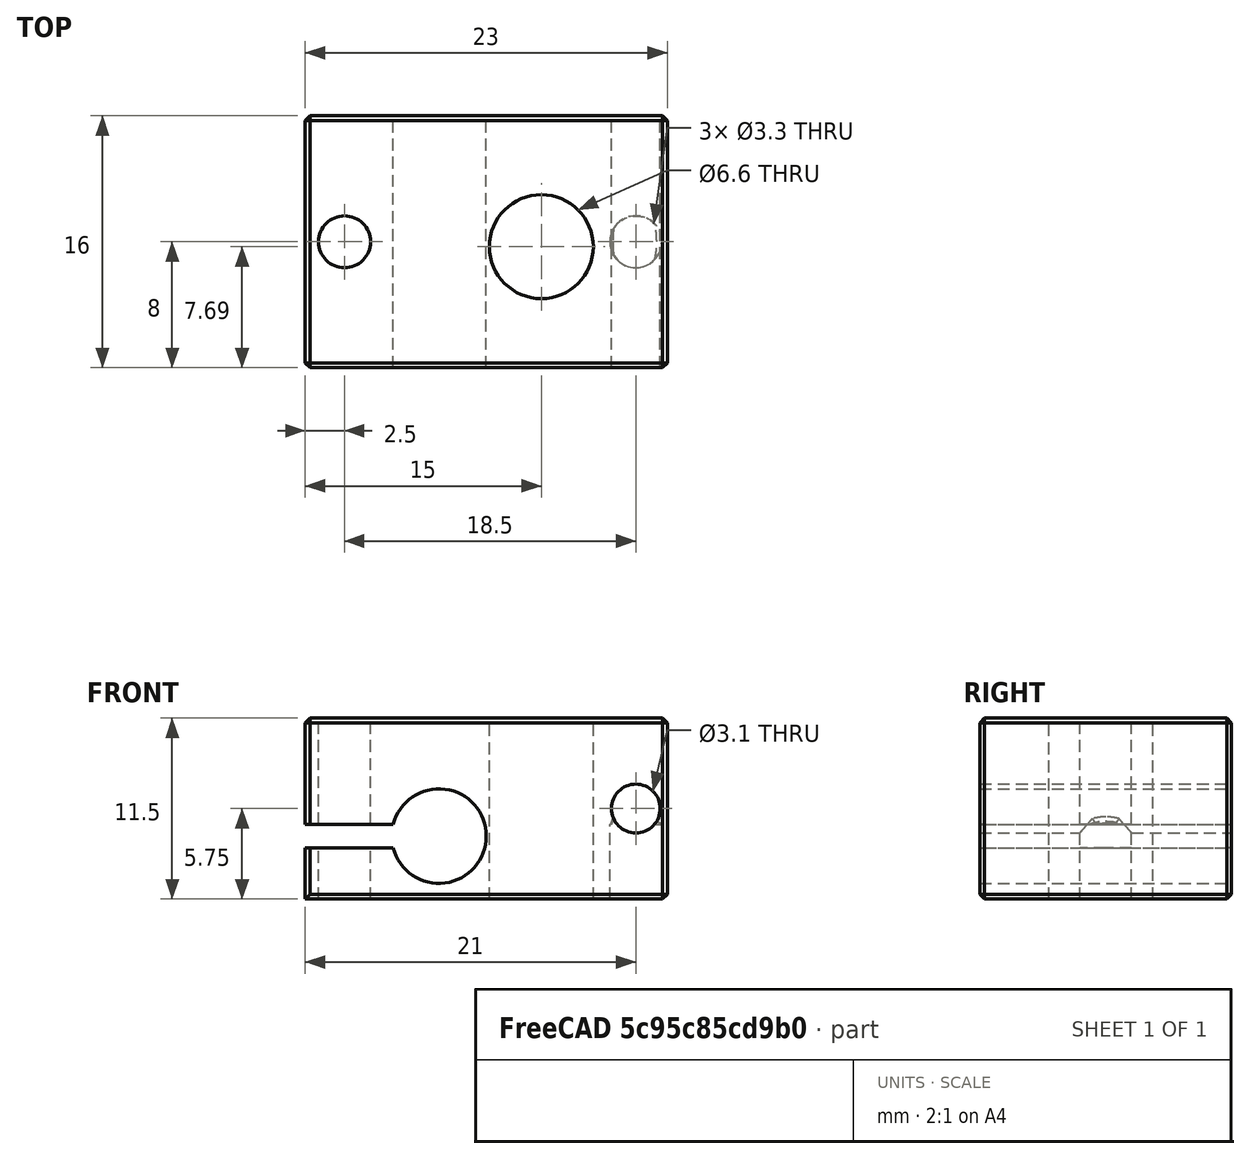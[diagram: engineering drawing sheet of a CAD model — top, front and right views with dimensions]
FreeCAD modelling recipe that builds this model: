
FCSTD DOCUMENT  (FreeCAD 0.20R29177 (Git))
Label: e3d_v6_cartridge
License: CreativeCommons Attribution-ShareAlike
LicenseURL: http://creativecommons.org/licenses/by-sa/4.0/
objects: Sketcher::SketchObject×2, Part::FeaturePython×1
note: 3 computed .brp shape members not serialized (recipe doc carries the construction recipe); baked Part::Feature solids carry a one-line shape summary decoded from their .brp

FEATURE [Part::FeaturePython] b_e3d_v6_cartridge_block_001_  label="Cartridge Block"  # a2plus imported part (geometry in sourceFile) (typed FeaturePython)
  Placement = pos=(-3.49976,0.309827,5.99999) rot=(0,0,1;0rad)
  a2p_Version = V0.1
  fixedPosition = false
  sourceFile = ./e3d_v6_cartridge_block.fcstd
  subassemblyImport = false
  timeLastImport = 1.54587e+09
  updateColors = true
FEATURE [Sketcher::SketchObject] Sketch001
  FullyConstrained = false
  MapMode = 2
  Placement = pos=(-3.49976,0.309827,5.99999) rot=(0,0,1;0rad)
  Support = -> [b_e3d_v6_cartridge_block_001_]
  sketch-geometry (4):
    g0: LineSegment StartX=-11.1906 StartY=7.68846 StartZ=0 EndX=11.1917 EndY=-7.70247 EndZ=0
    g1: LineSegment StartX=11.1972 StartY=7.69678 StartZ=0 EndX=-11.192 EndY=-7.69534 EndZ=0
    g2: LineSegment StartX=-11.5092 StartY=0 StartZ=0 EndX=11.4766 EndY=0 EndZ=0
    g3: Circle CenterX=3.45004 CenterY=0 CenterZ=0 NormalX=0 NormalY=0 NormalZ=1 AngleXU=0 Radius=0.875
  constraints (4):
    c: PointOnObject(g2,g-1)
    c: Horizontal(g2)
    c: PointOnObject(g3,g2)
    c: Radius(g3) = 0.875
FEATURE [Sketcher::SketchObject] Sketch
  ExternalGeometry = -> [Sketch001]
  FullyConstrained = false
  MapMode = 2
  Placement = pos=(-3.49976,0.309827,5.99999) rot=(0,0,1;0rad)
  Support = -> [Sketch001]
  sketch-geometry (3):
    g0: Circle CenterX=3.45004 CenterY=0 CenterZ=0 NormalX=0 NormalY=0 NormalZ=1 AngleXU=0 Radius=3.45
    g1: LineSegment StartX=3.45004 StartY=0 StartZ=0 EndX=3.45004 EndY=-5.28064 EndZ=0
    g2: LineSegment StartX=3.45004 StartY=0 StartZ=0 EndX=3.45004 EndY=-2.34562 EndZ=0
  constraints (7):
    c: PointOnObject(g0,g-1)
    c: Coincident(g1,g-3)
    c: Vertical(g1)
    c: Coincident(g2,g0)
    c: Vertical(g2)
    c: PointOnObject(g2,g1)
    c: Radius(g0) = 3.45
